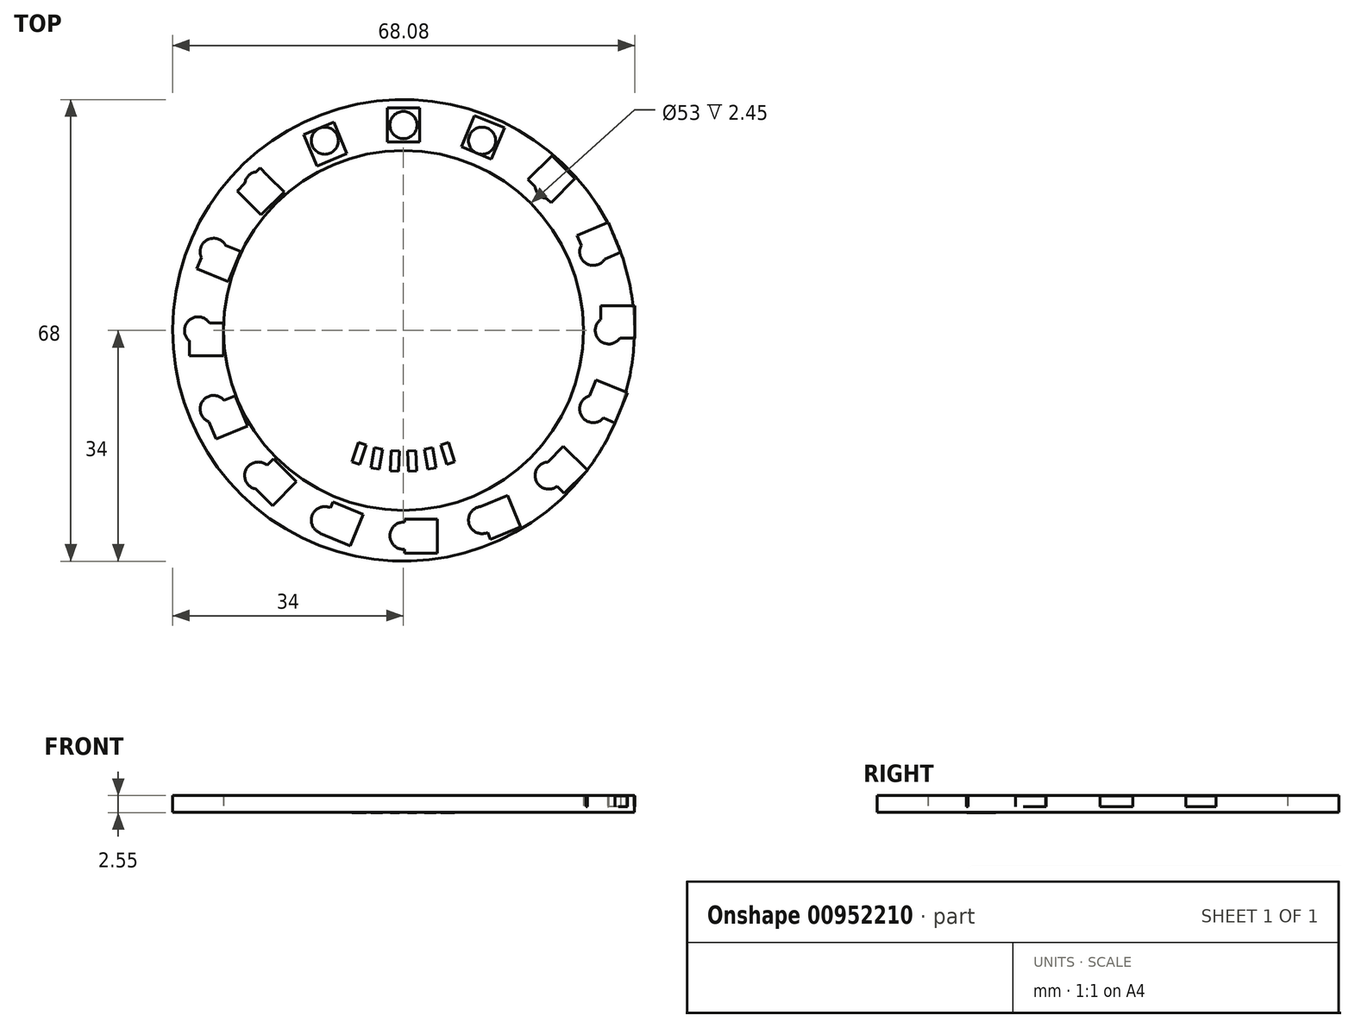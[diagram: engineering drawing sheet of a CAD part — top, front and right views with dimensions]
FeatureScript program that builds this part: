
annotation { "Feature Type Name" : "Feature", "Feature Type Description" : "" }
export const myFeature = defineFeature(function(context is Context, id is Id, definition is map)
    precondition{}
    {
        {
            var Q0;
            Q0=qCreatedBy(makeId("Top.planeOp"),FACE);
            var sketch = newSketch(context, id + "F0", { "sketchPlane" : qUnion([Q0])});
            skCircle(sketch, "E0", {"center": v(0, 0) * mm, "radius": 26.5 * mm});
            skCircle(sketch, "E1", {"center": v(0, 0) * mm, "radius": 34 * mm});
            skSolve(sketch);
        }
        {
            var Q0;
            Q0=makeQuery(id+"F0.imprint","IMPRINT",FACE,{"disambiguationData":[TD([[makeQuery(id+"F0.imprint","IMPRINT",EDGE,{"derivedFrom":sQuery(id+"F0.wireOp",EDGE,"E0")}),-1.0]])]});
            extrude(context, id + "F1", {"entities" : qUnion([Q0]), "depth" : 0.8 * mm});
        }
        {
            var Q0;
            Q0=makeQuery(id+"F1.opExtrude","CAP_FACE",FACE,{"disambiguationData":[OSD([sQuery(id+"F0.wireOp",EDGE,"E0"),sQuery(id+"F0.wireOp",EDGE,"E1")])],"isStart":false});
            var sketch = newSketch(context, id + "F2", { "sketchPlane" : qUnion([Q0])});
            skLineSegment(sketch, "E2", {"start": v(0, 34) * mm, "end": v(0, 26.5) * mm});
            skLineSegment(sketch, "E3.bottom", {"start": v(2.4, 27.75) * mm, "end": v(-2.4, 27.75) * mm});
            skLineSegment(sketch, "E3.top", {"start": v(2.4, 32.75) * mm, "end": v(-2.4, 32.75) * mm});
            skLineSegment(sketch, "E3.left", {"start": v(2.4, 27.75) * mm, "end": v(2.4, 32.75) * mm});
            skLineSegment(sketch, "E3.right", {"start": v(-2.4, 27.75) * mm, "end": v(-2.4, 32.75) * mm});
            skPoint(sketch, "E3.middle", {"position": v(0, 30.25) * mm});
            skLineSegment(sketch, "E4.1.0", {"start": v(-12.75, 24.22) * mm, "end": v(-14.67, 28.84) * mm});
            skLineSegment(sketch, "E4.1.1", {"start": v(-10.23, 30.68) * mm, "end": v(-14.67, 28.84) * mm});
            skLineSegment(sketch, "E4.1.2", {"start": v(-8.32, 26.06) * mm, "end": v(-10.23, 30.68) * mm});
            skLineSegment(sketch, "E4.1.3", {"start": v(-8.32, 26.06) * mm, "end": v(-12.75, 24.22) * mm});
            skLineSegment(sketch, "E4.2.0", {"start": v(-20.97, 17) * mm, "end": v(-24.5, 20.54) * mm});
            skLineSegment(sketch, "E4.2.1", {"start": v(-21.11, 23.93) * mm, "end": v(-24.5, 20.54) * mm});
            skLineSegment(sketch, "E4.2.2", {"start": v(-17.58, 20.4) * mm, "end": v(-21.11, 23.93) * mm});
            skLineSegment(sketch, "E4.2.3", {"start": v(-17.58, 20.4) * mm, "end": v(-20.97, 17) * mm});
            skLineSegment(sketch, "E4.3.0", {"start": v(-25.8, 7.19) * mm, "end": v(-30.42, 9.1) * mm});
            skLineSegment(sketch, "E4.3.1", {"start": v(-28.58, 13.54) * mm, "end": v(-30.42, 9.1) * mm});
            skLineSegment(sketch, "E4.3.2", {"start": v(-23.96, 11.62) * mm, "end": v(-28.58, 13.54) * mm});
            skLineSegment(sketch, "E4.3.3", {"start": v(-23.96, 11.62) * mm, "end": v(-25.8, 7.19) * mm});
            skLineSegment(sketch, "E4.4.0", {"start": v(-26.5, -3.73) * mm, "end": v(-31.5, -3.73) * mm});
            skLineSegment(sketch, "E4.4.1", {"start": v(-31.5, 1.07) * mm, "end": v(-31.5, -3.73) * mm});
            skLineSegment(sketch, "E4.4.2", {"start": v(-26.5, 1.07) * mm, "end": v(-31.5, 1.07) * mm});
            skLineSegment(sketch, "E4.4.3", {"start": v(-26.5, 1.07) * mm, "end": v(-26.5, -3.73) * mm});
            skLineSegment(sketch, "E4.5.0", {"start": v(-22.98, -14.08) * mm, "end": v(-27.6, -16) * mm});
            skLineSegment(sketch, "E4.5.1", {"start": v(-29.43, -11.56) * mm, "end": v(-27.6, -16) * mm});
            skLineSegment(sketch, "E4.5.2", {"start": v(-24.81, -9.65) * mm, "end": v(-29.43, -11.56) * mm});
            skLineSegment(sketch, "E4.5.3", {"start": v(-24.81, -9.65) * mm, "end": v(-22.98, -14.08) * mm});
            skLineSegment(sketch, "E4.6.0", {"start": v(-15.76, -22.3) * mm, "end": v(-19.3, -25.83) * mm});
            skLineSegment(sketch, "E4.6.1", {"start": v(-22.69, -22.44) * mm, "end": v(-19.3, -25.83) * mm});
            skLineSegment(sketch, "E4.6.2", {"start": v(-19.15, -18.9) * mm, "end": v(-22.69, -22.44) * mm});
            skLineSegment(sketch, "E4.6.3", {"start": v(-19.15, -18.9) * mm, "end": v(-15.76, -22.3) * mm});
            skLineSegment(sketch, "E4.7.0", {"start": v(-5.94, -27.13) * mm, "end": v(-7.85, -31.74) * mm});
            skLineSegment(sketch, "E4.7.1", {"start": v(-12.29, -29.9) * mm, "end": v(-7.85, -31.74) * mm});
            skLineSegment(sketch, "E4.7.2", {"start": v(-10.38, -25.29) * mm, "end": v(-12.29, -29.9) * mm});
            skLineSegment(sketch, "E4.7.3", {"start": v(-10.38, -25.29) * mm, "end": v(-5.94, -27.13) * mm});
            skLineSegment(sketch, "E4.8.0", {"start": v(4.97, -27.83) * mm, "end": v(4.97, -32.83) * mm});
            skLineSegment(sketch, "E4.8.1", {"start": v(0.17, -32.83) * mm, "end": v(4.97, -32.83) * mm});
            skLineSegment(sketch, "E4.8.2", {"start": v(0.17, -27.83) * mm, "end": v(0.17, -32.83) * mm});
            skLineSegment(sketch, "E4.8.3", {"start": v(0.17, -27.83) * mm, "end": v(4.97, -27.83) * mm});
            skLineSegment(sketch, "E4.9.0", {"start": v(15.33, -24.3) * mm, "end": v(17.24, -28.92) * mm});
            skLineSegment(sketch, "E4.9.1", {"start": v(12.8, -30.76) * mm, "end": v(17.24, -28.92) * mm});
            skLineSegment(sketch, "E4.9.2", {"start": v(10.9, -26.14) * mm, "end": v(12.8, -30.76) * mm});
            skLineSegment(sketch, "E4.9.3", {"start": v(10.9, -26.14) * mm, "end": v(15.33, -24.3) * mm});
            skLineSegment(sketch, "E4.10.0", {"start": v(23.55, -17.08) * mm, "end": v(27.08, -20.62) * mm});
            skLineSegment(sketch, "E4.10.1", {"start": v(23.69, -24.01) * mm, "end": v(27.08, -20.62) * mm});
            skLineSegment(sketch, "E4.10.2", {"start": v(20.15, -20.48) * mm, "end": v(23.69, -24.01) * mm});
            skLineSegment(sketch, "E4.10.3", {"start": v(20.15, -20.48) * mm, "end": v(23.55, -17.08) * mm});
            skLineSegment(sketch, "E4.11.0", {"start": v(28.37, -7.27) * mm, "end": v(33, -9.18) * mm});
            skLineSegment(sketch, "E4.11.1", {"start": v(31.16, -13.62) * mm, "end": v(33, -9.18) * mm});
            skLineSegment(sketch, "E4.11.2", {"start": v(26.54, -11.7) * mm, "end": v(31.16, -13.62) * mm});
            skLineSegment(sketch, "E4.11.3", {"start": v(26.54, -11.7) * mm, "end": v(28.37, -7.27) * mm});
            skLineSegment(sketch, "E4.12.0", {"start": v(29.08, 3.65) * mm, "end": v(34.08, 3.65) * mm});
            skLineSegment(sketch, "E4.12.1", {"start": v(34.08, -1.15) * mm, "end": v(34.08, 3.65) * mm});
            skLineSegment(sketch, "E4.12.2", {"start": v(29.08, -1.15) * mm, "end": v(34.08, -1.15) * mm});
            skLineSegment(sketch, "E4.12.3", {"start": v(29.08, -1.15) * mm, "end": v(29.08, 3.65) * mm});
            skLineSegment(sketch, "E4.13.0", {"start": v(25.55, 14) * mm, "end": v(30.17, 15.92) * mm});
            skLineSegment(sketch, "E4.13.1", {"start": v(32, 11.48) * mm, "end": v(30.17, 15.92) * mm});
            skLineSegment(sketch, "E4.13.2", {"start": v(27.39, 9.57) * mm, "end": v(32, 11.48) * mm});
            skLineSegment(sketch, "E4.13.3", {"start": v(27.39, 9.57) * mm, "end": v(25.55, 14) * mm});
            skLineSegment(sketch, "E4.14.0", {"start": v(18.33, 22.22) * mm, "end": v(21.87, 25.75) * mm});
            skLineSegment(sketch, "E4.14.1", {"start": v(25.26, 22.36) * mm, "end": v(21.87, 25.75) * mm});
            skLineSegment(sketch, "E4.14.2", {"start": v(21.72, 18.82) * mm, "end": v(25.26, 22.36) * mm});
            skLineSegment(sketch, "E4.14.3", {"start": v(21.72, 18.82) * mm, "end": v(18.33, 22.22) * mm});
            skLineSegment(sketch, "E4.15.0", {"start": v(8.52, 27.05) * mm, "end": v(10.43, 31.67) * mm});
            skLineSegment(sketch, "E4.15.1", {"start": v(14.86, 29.83) * mm, "end": v(10.43, 31.67) * mm});
            skLineSegment(sketch, "E4.15.2", {"start": v(12.95, 25.2) * mm, "end": v(14.86, 29.83) * mm});
            skLineSegment(sketch, "E4.15.3", {"start": v(12.95, 25.2) * mm, "end": v(8.52, 27.05) * mm});
            skPoint(sketch, "E4.center", {"position": v(1.29, -0.04) * mm});
            skCircle(sketch, "E5", {"center": v(0, 30.25) * mm, "radius": 2 * mm});
            skCircle(sketch, "E6.1.0", {"center": v(-11.58, 27.95) * mm, "radius": 2 * mm});
            skCircle(sketch, "E6.2.0", {"center": v(-21.39, 21.39) * mm, "radius": 2 * mm});
            skCircle(sketch, "E6.3.0", {"center": v(-27.95, 11.58) * mm, "radius": 2 * mm});
            skCircle(sketch, "E6.4.0", {"center": v(-30.25, 0) * mm, "radius": 2 * mm});
            skCircle(sketch, "E6.5.0", {"center": v(-27.95, -11.58) * mm, "radius": 2 * mm});
            skCircle(sketch, "E6.6.0", {"center": v(-21.39, -21.39) * mm, "radius": 2 * mm});
            skCircle(sketch, "E6.7.0", {"center": v(-11.58, -27.95) * mm, "radius": 2 * mm});
            skCircle(sketch, "E6.8.0", {"center": v(0, -30.25) * mm, "radius": 2 * mm});
            skCircle(sketch, "E6.9.0", {"center": v(11.58, -27.95) * mm, "radius": 2 * mm});
            skCircle(sketch, "E6.10.0", {"center": v(21.39, -21.39) * mm, "radius": 2 * mm});
            skCircle(sketch, "E6.11.0", {"center": v(27.95, -11.58) * mm, "radius": 2 * mm});
            skCircle(sketch, "E6.12.0", {"center": v(30.25, 0) * mm, "radius": 2 * mm});
            skCircle(sketch, "E6.13.0", {"center": v(27.95, 11.58) * mm, "radius": 2 * mm});
            skCircle(sketch, "E6.14.0", {"center": v(21.39, 21.39) * mm, "radius": 2 * mm});
            skCircle(sketch, "E6.15.0", {"center": v(11.58, 27.95) * mm, "radius": 2 * mm});
            skPoint(sketch, "E6.center", {"position": v(0, 0) * mm});
            skSolve(sketch);
        }
        {
            var Q0;
            Q0=qSketchRegion(id+"F2",true);
            extrude(context, id + "F3", {"entities" : qUnion([Q0]), "operationType" : NewBodyOperationType.ADD, "depth" : 1.6 * mm});
        }
        {
            var Q0;
            Q0=makeQuery(id+"F3.boolean.opBoolean","SPLIT",FACE,{"disambiguationData":[TD([makeQuery(id+"F3.opExtrude","SWEPT_FACE",FACE,{"disambiguationData":[OSD([sQuery(id+"F2.wireOp",EDGE,"E6.3.0")])]})])],"derivedFrom":makeQuery(id+"F1.opExtrude","CAP_FACE",FACE,{"disambiguationData":[OSD([sQuery(id+"F0.wireOp",EDGE,"E0"),sQuery(id+"F0.wireOp",EDGE,"E1")])],"isStart":false})});
            var Q1;
            Q1=makeQuery(id+"F3.boolean.opBoolean","SPLIT",FACE,{"disambiguationData":[TD([makeQuery(id+"F3.opExtrude","SWEPT_FACE",FACE,{"disambiguationData":[OSD([sQuery(id+"F2.wireOp",EDGE,"E6.2.0")])]})])],"derivedFrom":makeQuery(id+"F1.opExtrude","CAP_FACE",FACE,{"disambiguationData":[OSD([sQuery(id+"F0.wireOp",EDGE,"E0"),sQuery(id+"F0.wireOp",EDGE,"E1")])],"isStart":false})});
            var Q2;
            Q2=makeQuery(id+"F3.boolean.opBoolean","SPLIT",FACE,{"disambiguationData":[TD([makeQuery(id+"F3.opExtrude","SWEPT_FACE",FACE,{"disambiguationData":[OSD([sQuery(id+"F2.wireOp",EDGE,"E6.1.0")])]})])],"derivedFrom":makeQuery(id+"F1.opExtrude","CAP_FACE",FACE,{"disambiguationData":[OSD([sQuery(id+"F0.wireOp",EDGE,"E0"),sQuery(id+"F0.wireOp",EDGE,"E1")])],"isStart":false})});
            var Q3;
            Q3=makeQuery(id+"F3.boolean.opBoolean","SPLIT",FACE,{"disambiguationData":[TD([makeQuery(id+"F3.opExtrude","SWEPT_FACE",FACE,{"disambiguationData":[OSD([sQuery(id+"F2.wireOp",EDGE,"E5")])]})])],"derivedFrom":makeQuery(id+"F1.opExtrude","CAP_FACE",FACE,{"disambiguationData":[OSD([sQuery(id+"F0.wireOp",EDGE,"E0"),sQuery(id+"F0.wireOp",EDGE,"E1")])],"isStart":false})});
            var Q4;
            Q4=makeQuery(id+"F3.boolean.opBoolean","SPLIT",FACE,{"disambiguationData":[TD([makeQuery(id+"F3.opExtrude","SWEPT_FACE",FACE,{"disambiguationData":[OSD([sQuery(id+"F2.wireOp",EDGE,"E6.15.0")])]})])],"derivedFrom":makeQuery(id+"F1.opExtrude","CAP_FACE",FACE,{"disambiguationData":[OSD([sQuery(id+"F0.wireOp",EDGE,"E0"),sQuery(id+"F0.wireOp",EDGE,"E1")])],"isStart":false})});
            var Q5;
            Q5=makeQuery(id+"F3.boolean.opBoolean","SPLIT",FACE,{"disambiguationData":[TD([makeQuery(id+"F3.opExtrude","SWEPT_FACE",FACE,{"disambiguationData":[OSD([sQuery(id+"F2.wireOp",EDGE,"E6.4.0")])]})])],"derivedFrom":makeQuery(id+"F1.opExtrude","CAP_FACE",FACE,{"disambiguationData":[OSD([sQuery(id+"F0.wireOp",EDGE,"E0"),sQuery(id+"F0.wireOp",EDGE,"E1")])],"isStart":false})});
            var Q6;
            Q6=makeQuery(id+"F3.boolean.opBoolean","SPLIT",FACE,{"disambiguationData":[TD([makeQuery(id+"F3.opExtrude","SWEPT_FACE",FACE,{"disambiguationData":[OSD([sQuery(id+"F2.wireOp",EDGE,"E6.5.0")])]})])],"derivedFrom":makeQuery(id+"F1.opExtrude","CAP_FACE",FACE,{"disambiguationData":[OSD([sQuery(id+"F0.wireOp",EDGE,"E0"),sQuery(id+"F0.wireOp",EDGE,"E1")])],"isStart":false})});
            var Q7;
            Q7=makeQuery(id+"F3.boolean.opBoolean","SPLIT",FACE,{"disambiguationData":[TD([makeQuery(id+"F3.opExtrude","SWEPT_FACE",FACE,{"disambiguationData":[OSD([sQuery(id+"F2.wireOp",EDGE,"E6.6.0")])]})])],"derivedFrom":makeQuery(id+"F1.opExtrude","CAP_FACE",FACE,{"disambiguationData":[OSD([sQuery(id+"F0.wireOp",EDGE,"E0"),sQuery(id+"F0.wireOp",EDGE,"E1")])],"isStart":false})});
            var Q8;
            Q8=makeQuery(id+"F3.boolean.opBoolean","SPLIT",FACE,{"disambiguationData":[TD([makeQuery(id+"F3.opExtrude","SWEPT_FACE",FACE,{"disambiguationData":[OSD([sQuery(id+"F2.wireOp",EDGE,"E6.7.0")])]})])],"derivedFrom":makeQuery(id+"F1.opExtrude","CAP_FACE",FACE,{"disambiguationData":[OSD([sQuery(id+"F0.wireOp",EDGE,"E0"),sQuery(id+"F0.wireOp",EDGE,"E1")])],"isStart":false})});
            var Q9;
            Q9=makeQuery(id+"F3.boolean.opBoolean","SPLIT",FACE,{"disambiguationData":[TD([makeQuery(id+"F3.opExtrude","SWEPT_FACE",FACE,{"disambiguationData":[OSD([sQuery(id+"F2.wireOp",EDGE,"E6.8.0")])]})])],"derivedFrom":makeQuery(id+"F1.opExtrude","CAP_FACE",FACE,{"disambiguationData":[OSD([sQuery(id+"F0.wireOp",EDGE,"E0"),sQuery(id+"F0.wireOp",EDGE,"E1")])],"isStart":false})});
            var Q10;
            Q10=makeQuery(id+"F3.boolean.opBoolean","SPLIT",FACE,{"disambiguationData":[TD([makeQuery(id+"F3.opExtrude","SWEPT_FACE",FACE,{"disambiguationData":[OSD([sQuery(id+"F2.wireOp",EDGE,"E6.9.0")])]})])],"derivedFrom":makeQuery(id+"F1.opExtrude","CAP_FACE",FACE,{"disambiguationData":[OSD([sQuery(id+"F0.wireOp",EDGE,"E0"),sQuery(id+"F0.wireOp",EDGE,"E1")])],"isStart":false})});
            var Q11;
            Q11=makeQuery(id+"F3.boolean.opBoolean","SPLIT",FACE,{"disambiguationData":[TD([makeQuery(id+"F3.opExtrude","SWEPT_FACE",FACE,{"disambiguationData":[OSD([sQuery(id+"F2.wireOp",EDGE,"E6.10.0")])]})])],"derivedFrom":makeQuery(id+"F1.opExtrude","CAP_FACE",FACE,{"disambiguationData":[OSD([sQuery(id+"F0.wireOp",EDGE,"E0"),sQuery(id+"F0.wireOp",EDGE,"E1")])],"isStart":false})});
            var Q12;
            Q12=makeQuery(id+"F3.boolean.opBoolean","SPLIT",FACE,{"disambiguationData":[TD([makeQuery(id+"F3.opExtrude","SWEPT_FACE",FACE,{"disambiguationData":[OSD([sQuery(id+"F2.wireOp",EDGE,"E6.11.0")])]})])],"derivedFrom":makeQuery(id+"F1.opExtrude","CAP_FACE",FACE,{"disambiguationData":[OSD([sQuery(id+"F0.wireOp",EDGE,"E0"),sQuery(id+"F0.wireOp",EDGE,"E1")])],"isStart":false})});
            var Q13;
            Q13=makeQuery(id+"F3.boolean.opBoolean","SPLIT",FACE,{"disambiguationData":[TD([makeQuery(id+"F3.opExtrude","SWEPT_FACE",FACE,{"disambiguationData":[OSD([sQuery(id+"F2.wireOp",EDGE,"E6.12.0")])]})])],"derivedFrom":makeQuery(id+"F1.opExtrude","CAP_FACE",FACE,{"disambiguationData":[OSD([sQuery(id+"F0.wireOp",EDGE,"E0"),sQuery(id+"F0.wireOp",EDGE,"E1")])],"isStart":false})});
            var Q14;
            Q14=makeQuery(id+"F3.boolean.opBoolean","SPLIT",FACE,{"disambiguationData":[TD([makeQuery(id+"F3.opExtrude","SWEPT_FACE",FACE,{"disambiguationData":[OSD([sQuery(id+"F2.wireOp",EDGE,"E6.14.0")])]})])],"derivedFrom":makeQuery(id+"F1.opExtrude","CAP_FACE",FACE,{"disambiguationData":[OSD([sQuery(id+"F0.wireOp",EDGE,"E0"),sQuery(id+"F0.wireOp",EDGE,"E1")])],"isStart":false})});
            var Q15;
            Q15=makeQuery(id+"F3.boolean.opBoolean","SPLIT",FACE,{"disambiguationData":[TD([makeQuery(id+"F3.opExtrude","SWEPT_FACE",FACE,{"disambiguationData":[OSD([sQuery(id+"F2.wireOp",EDGE,"E6.13.0")])]})])],"derivedFrom":makeQuery(id+"F1.opExtrude","CAP_FACE",FACE,{"disambiguationData":[OSD([sQuery(id+"F0.wireOp",EDGE,"E0"),sQuery(id+"F0.wireOp",EDGE,"E1")])],"isStart":false})});
            extrude(context, id + "F4", {"entities" : qUnion([Q0, Q1, Q2, Q3, Q4, Q5, Q6, Q7, Q8, Q9, Q10, Q11, Q12, Q13, Q14, Q15]), "operationType" : NewBodyOperationType.ADD, "depth" : 1.65 * mm});
        }
        {
            var Q0;
            Q0=makeQuery(id+"F1.opExtrude","CAP_FACE",FACE,{"disambiguationData":[OSD([sQuery(id+"F0.wireOp",EDGE,"E0"),sQuery(id+"F0.wireOp",EDGE,"E1")])],"isStart":true});
            var sketch = newSketch(context, id + "F5", { "sketchPlane" : qUnion([Q0])});
            skLineSegment(sketch, "E7", {"start": v(0, 0) * mm, "end": v(5.49, 16.9) * mm, "construction": true});
            skLineSegment(sketch, "E8.bottom", {"start": v(6.42, 19.75) * mm, "end": v(7.56, 19.38) * mm});
            skLineSegment(sketch, "E8.top", {"start": v(5.49, 16.9) * mm, "end": v(6.63, 16.52) * mm});
            skLineSegment(sketch, "E8.left", {"start": v(6.42, 19.75) * mm, "end": v(5.49, 16.9) * mm});
            skLineSegment(sketch, "E8.right", {"start": v(7.56, 19.38) * mm, "end": v(6.63, 16.52) * mm});
            skLineSegment(sketch, "E9", {"start": v(0, 0) * mm, "end": v(0.62, 17.75) * mm, "construction": true});
            skLineSegment(sketch, "E10.bottom", {"start": v(0.72, 20.75) * mm, "end": v(1.92, 20.7) * mm});
            skLineSegment(sketch, "E10.top", {"start": v(0.62, 17.75) * mm, "end": v(1.82, 17.71) * mm});
            skLineSegment(sketch, "E10.left", {"start": v(0.72, 20.75) * mm, "end": v(0.62, 17.75) * mm});
            skLineSegment(sketch, "E10.right", {"start": v(1.92, 20.7) * mm, "end": v(1.82, 17.71) * mm});
            skLineSegment(sketch, "E11", {"start": v(0, 0) * mm, "end": v(3.08, 17.5) * mm, "construction": true});
            skLineSegment(sketch, "E12.bottom", {"start": v(3.6, 20.45) * mm, "end": v(4.79, 20.24) * mm});
            skLineSegment(sketch, "E12.top", {"start": v(3.08, 17.5) * mm, "end": v(4.27, 17.29) * mm});
            skLineSegment(sketch, "E12.left", {"start": v(3.6, 20.45) * mm, "end": v(3.08, 17.5) * mm});
            skLineSegment(sketch, "E12.right", {"start": v(4.79, 20.24) * mm, "end": v(4.27, 17.29) * mm});
            skLineSegment(sketch, "E13.MirrorCS", {"start": v(-0.72, 20.75) * mm, "end": v(-1.92, 20.7) * mm});
            skLineSegment(sketch, "E14.MirrorCS", {"start": v(-0.62, 17.75) * mm, "end": v(-1.82, 17.71) * mm});
            skLineSegment(sketch, "E15.MirrorCS", {"start": v(-1.92, 20.7) * mm, "end": v(-1.82, 17.71) * mm});
            skLineSegment(sketch, "E16.MirrorCS", {"start": v(0, 0) * mm, "end": v(-0.62, 17.75) * mm, "construction": true});
            skLineSegment(sketch, "E17.MirrorCS", {"start": v(-3.6, 20.45) * mm, "end": v(-4.79, 20.24) * mm});
            skLineSegment(sketch, "E18.MirrorCS", {"start": v(-4.79, 20.24) * mm, "end": v(-4.27, 17.29) * mm});
            skLineSegment(sketch, "E19.MirrorCS", {"start": v(-3.08, 17.5) * mm, "end": v(-4.27, 17.29) * mm});
            skLineSegment(sketch, "E20.MirrorCS", {"start": v(-6.42, 19.75) * mm, "end": v(-7.56, 19.38) * mm});
            skLineSegment(sketch, "E21.MirrorCS", {"start": v(-7.56, 19.38) * mm, "end": v(-6.63, 16.52) * mm});
            skLineSegment(sketch, "E22.MirrorCS", {"start": v(-5.49, 16.9) * mm, "end": v(-6.63, 16.52) * mm});
            skLineSegment(sketch, "E23.MirrorCS", {"start": v(-6.42, 19.75) * mm, "end": v(-5.49, 16.9) * mm});
            skLineSegment(sketch, "E24.MirrorCS", {"start": v(-3.6, 20.45) * mm, "end": v(-3.08, 17.5) * mm});
            skLineSegment(sketch, "E25.MirrorCS", {"start": v(-0.72, 20.75) * mm, "end": v(-0.62, 17.75) * mm});
            skSolve(sketch);
        }
        {
            var Q0;
            Q0=qSketchRegion(id+"F5",true);
            extrude(context, id + "F6", {"entities" : qUnion([Q0]), "operationType" : NewBodyOperationType.ADD, "depth" : .1 * mm});
        }
    });
